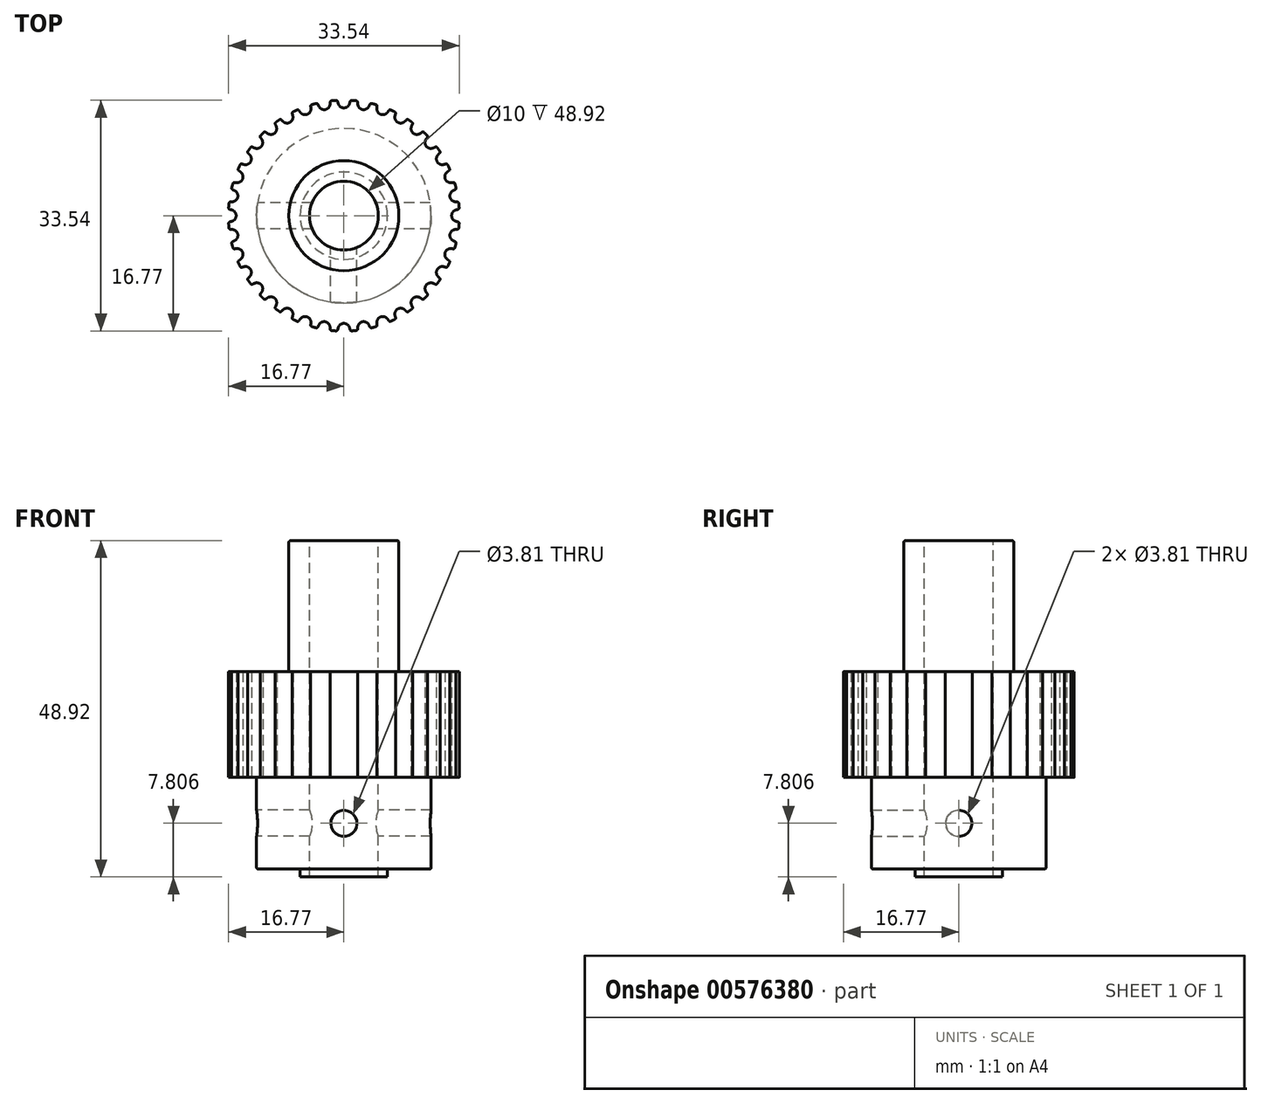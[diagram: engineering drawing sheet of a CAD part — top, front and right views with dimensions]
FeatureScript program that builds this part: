
annotation { "Feature Type Name" : "Feature", "Feature Type Description" : "" }
export const myFeature = defineFeature(function(context is Context, id is Id, definition is map)
    precondition{}
    {
        {
            assignVariable(context, id + "F0", {"name" : "teeth", "anyValue" : 36});
        }
        {
            assignVariable(context, id + "F1", {"name" : "width", "anyValue" : 15.4 * mm});
        }
        {
            var Q0;
            Q0=qCreatedBy(makeId("Top.planeOp"),FACE);
            var sketch = newSketch(context, id + "F2", { "sketchPlane" : qUnion([Q0])});
            skLineSegment(sketch, "E0", {"start": v(0, 0) * mm, "end": v(0, 15.67) * mm, "construction": true});
            skArc(sketch, "E1", {"start": v(4.3, 16.25) * mm, "mid": v(0, 16.8) * mm, "end": v(-4.3, 16.25) * mm, "construction": true});
            skArc(sketch, "E2", {"start": v(0, 15.67) * mm, "mid": v(0.46, 15.8) * mm, "end": v(0.77, 16.17) * mm});
            skLineSegment(sketch, "E3", {"start": v(0, 15.67) * mm, "end": v(0, 16.8) * mm, "construction": true});
            skLineSegment(sketch, "E4", {"start": v(0, 16.8) * mm, "end": v(0, 17.19) * mm, "construction": true});
            skArc(sketch, "E5", {"start": v(1.5, 17.12) * mm, "mid": v(0, 17.19) * mm, "end": v(-1.5, 17.12) * mm, "construction": true});
            skLineSegment(sketch, "E6", {"start": v(1.46, 16.74) * mm, "end": v(0, 0) * mm});
            skLineSegment(sketch, "E7", {"start": v(0, 0) * mm, "end": v(-1.46, 16.74) * mm});
            skArc(sketch, "E8", {"start": v(1.16, 16.77) * mm, "mid": v(0.98, 16.71) * mm, "end": v(0.9, 16.56) * mm});
            skArc(sketch, "E9", {"start": v(0.77, 16.17) * mm, "mid": v(0.85, 16.36) * mm, "end": v(0.9, 16.56) * mm});
            skArc(sketch, "E10.MirrorCS", {"start": v(0, 15.67) * mm, "mid": v(-0.46, 15.8) * mm, "end": v(-0.77, 16.17) * mm});
            skArc(sketch, "E11.MirrorCS", {"start": v(-0.77, 16.17) * mm, "mid": v(-0.85, 16.36) * mm, "end": v(-0.9, 16.56) * mm});
            skArc(sketch, "E12.MirrorCS", {"start": v(-1.16, 16.77) * mm, "mid": v(-0.98, 16.71) * mm, "end": v(-0.9, 16.56) * mm});
            skArc(sketch, "E13", {"start": v(0, 16.8) * mm, "mid": v(-0.3, 16.8) * mm, "end": v(-0.6, 16.8) * mm, "construction": true});
            skArc(sketch, "E14", {"start": v(4.23, 15.09) * mm, "mid": v(0, 15.67) * mm, "end": v(-4.23, 15.09) * mm, "construction": true});
            skArc(sketch, "E15", {"start": v(-1.16, 16.77) * mm, "mid": v(-1.31, 16.76) * mm, "end": v(-1.46, 16.74) * mm});
            skArc(sketch, "E16", {"start": v(1.16, 16.77) * mm, "mid": v(1.31, 16.76) * mm, "end": v(1.46, 16.74) * mm});
            skPoint(sketch, "E17", {"position": v(0, 15.67) * mm});
            skSolve(sketch);
        }
        {
            var Q0;
            Q0=makeQuery(id+"F2.imprint","IMPRINT",FACE,{"disambiguationData":[TD([[makeQuery(id+"F2.imprint","IMPRINT",EDGE,{"derivedFrom":sQuery(id+"F2.wireOp",EDGE,"E2")}),-1.0]])]});
            var Q1;
            {var subQ1=sQuery(id+"F2.wireOp",EDGE,"N9a9pOVT-NxnP-9PMo-Yz0L-ytRW1WlfzG62");Q1=makeQuery(id+"F2.imprint","IMPRINT",FACE,{"disambiguationData":[TD([[makeQuery(id+"F2.imprint","IMPRINT",EDGE,{"derivedFrom":subQ1}),-1.0]])]});}
            var Q2;
            {var subQ0=sQuery(id+"F2.wireOp",EDGE,"E6");Q2=makeQuery(id+"F2.imprint","IMPRINT",FACE,{"disambiguationData":[TD([[makeQuery(id+"F2.imprint","IMPRINT",EDGE,{"derivedFrom":subQ0}),-1.0]])]});}
            extrude(context, id + "F3", {"entities" : qUnion([Q0, Q1, Q2]), "depth" : (getVariable(context, 'width')), "offsetDistance" : 25 * mm, "symmetric" : true});
        }
        {
            var Q0;
            Q0=makeQuery(id+"F3.opExtrude","SWEPT_BODY",BODY,{"disambiguationData":[OSD([sQuery(id+"F2.wireOp",EDGE,"E1"),sQuery(id+"F2.wireOp",EDGE,"E2"),sQuery(id+"F2.wireOp",EDGE,"WtW3y5By-gfdo-wMA2-XeKf-OYMCoWhlFWBV"),sQuery(id+"F2.wireOp",EDGE,"E6"),sQuery(id+"F2.wireOp",EDGE,"E7"),sQuery(id+"F2.wireOp",EDGE,"N9a9pOVT-NxnP-9PMo-Yz0L-ytRW1WlfzG62"),sQuery(id+"F2.wireOp",EDGE,"E8"),sQuery(id+"F2.wireOp",EDGE,"E9"),sQuery(id+"F2.wireOp",EDGE,"E10.MirrorCS"),sQuery(id+"F2.wireOp",EDGE,"E11.MirrorCS"),sQuery(id+"F2.wireOp",EDGE,"E12.MirrorCS")])]});
            var Q1;
            Q1=makeQuery(id+"F3.opExtrude","SWEPT_EDGE",EDGE,{"disambiguationData":[OSD([sQuery(id+"F2.wireOp",EDGE,"E6"),sQuery(id+"F2.wireOp",EDGE,"E7")])]});
            circularPattern(context, id + "F4", {"operationType" : NewBodyOperationType.ADD, "entities" : qUnion([Q0]), "axis" : qUnion([Q1]), "angle" : 360 * degree, "instanceCount" : getVariable(context, 'teeth'), "equalSpace" : true, "computeTransformsWithoutBuiltin" : true});
        }
        {
            var Q0;
            {var subQ0=makeQuery(id+"F3.opExtrude","CAP_FACE",FACE,{"disambiguationData":[OSD([sQuery(id+"F2.wireOp",EDGE,"E2"),sQuery(id+"F2.wireOp",EDGE,"E6"),sQuery(id+"F2.wireOp",EDGE,"E7"),sQuery(id+"F2.wireOp",EDGE,"E8"),sQuery(id+"F2.wireOp",EDGE,"E9"),sQuery(id+"F2.wireOp",EDGE,"E10.MirrorCS"),sQuery(id+"F2.wireOp",EDGE,"E11.MirrorCS"),sQuery(id+"F2.wireOp",EDGE,"E12.MirrorCS"),sQuery(id+"F2.wireOp",EDGE,"E15"),sQuery(id+"F2.wireOp",EDGE,"E16")])],"isStart":true});Q0=makeQuery(id+"F4.boolean.opBoolean","MERGE",FACE,{"derivedFrom":[subQ0,makeQuery(id+"F4.opPattern","COPY",FACE,{"derivedFrom":subQ0,"instanceName":"1"}),makeQuery(id+"F4.opPattern","COPY",FACE,{"derivedFrom":subQ0,"instanceName":"2"}),makeQuery(id+"F4.opPattern","COPY",FACE,{"derivedFrom":subQ0,"instanceName":"3"}),makeQuery(id+"F4.opPattern","COPY",FACE,{"derivedFrom":subQ0,"instanceName":"4"}),makeQuery(id+"F4.opPattern","COPY",FACE,{"derivedFrom":subQ0,"instanceName":"5"}),makeQuery(id+"F4.opPattern","COPY",FACE,{"derivedFrom":subQ0,"instanceName":"6"}),makeQuery(id+"F4.opPattern","COPY",FACE,{"derivedFrom":subQ0,"instanceName":"7"}),makeQuery(id+"F4.opPattern","COPY",FACE,{"derivedFrom":subQ0,"instanceName":"8"}),makeQuery(id+"F4.opPattern","COPY",FACE,{"derivedFrom":subQ0,"instanceName":"9"}),makeQuery(id+"F4.opPattern","COPY",FACE,{"derivedFrom":subQ0,"instanceName":"10"}),makeQuery(id+"F4.opPattern","COPY",FACE,{"derivedFrom":subQ0,"instanceName":"11"}),makeQuery(id+"F4.opPattern","COPY",FACE,{"derivedFrom":subQ0,"instanceName":"12"}),makeQuery(id+"F4.opPattern","COPY",FACE,{"derivedFrom":subQ0,"instanceName":"13"}),makeQuery(id+"F4.opPattern","COPY",FACE,{"derivedFrom":subQ0,"instanceName":"14"}),makeQuery(id+"F4.opPattern","COPY",FACE,{"derivedFrom":subQ0,"instanceName":"15"}),makeQuery(id+"F4.opPattern","COPY",FACE,{"derivedFrom":subQ0,"instanceName":"16"}),makeQuery(id+"F4.opPattern","COPY",FACE,{"derivedFrom":subQ0,"instanceName":"17"}),makeQuery(id+"F4.opPattern","COPY",FACE,{"derivedFrom":subQ0,"instanceName":"18"}),makeQuery(id+"F4.opPattern","COPY",FACE,{"derivedFrom":subQ0,"instanceName":"19"}),makeQuery(id+"F4.opPattern","COPY",FACE,{"derivedFrom":subQ0,"instanceName":"20"}),makeQuery(id+"F4.opPattern","COPY",FACE,{"derivedFrom":subQ0,"instanceName":"21"}),makeQuery(id+"F4.opPattern","COPY",FACE,{"derivedFrom":subQ0,"instanceName":"22"}),makeQuery(id+"F4.opPattern","COPY",FACE,{"derivedFrom":subQ0,"instanceName":"23"}),makeQuery(id+"F4.opPattern","COPY",FACE,{"derivedFrom":subQ0,"instanceName":"24"}),makeQuery(id+"F4.opPattern","COPY",FACE,{"derivedFrom":subQ0,"instanceName":"25"}),makeQuery(id+"F4.opPattern","COPY",FACE,{"derivedFrom":subQ0,"instanceName":"26"}),makeQuery(id+"F4.opPattern","COPY",FACE,{"derivedFrom":subQ0,"instanceName":"27"}),makeQuery(id+"F4.opPattern","COPY",FACE,{"derivedFrom":subQ0,"instanceName":"28"}),makeQuery(id+"F4.opPattern","COPY",FACE,{"derivedFrom":subQ0,"instanceName":"29"}),makeQuery(id+"F4.opPattern","COPY",FACE,{"derivedFrom":subQ0,"instanceName":"30"}),makeQuery(id+"F4.opPattern","COPY",FACE,{"derivedFrom":subQ0,"instanceName":"31"}),makeQuery(id+"F4.opPattern","COPY",FACE,{"derivedFrom":subQ0,"instanceName":"32"}),makeQuery(id+"F4.opPattern","COPY",FACE,{"derivedFrom":subQ0,"instanceName":"33"}),makeQuery(id+"F4.opPattern","COPY",FACE,{"derivedFrom":subQ0,"instanceName":"34"}),makeQuery(id+"F4.opPattern","COPY",FACE,{"derivedFrom":subQ0,"instanceName":"35"})]});}
            var sketch = newSketch(context, id + "F5", { "sketchPlane" : qUnion([Q0])});
            skCircle(sketch, "E18", {"center": v(0, 0) * mm, "radius": 12.7 * mm});
            skSolve(sketch);
        }
        {
            var Q0;
            Q0=qSketchRegion(id+"F5",true);
            extrude(context, id + "F6", {"entities" : qUnion([Q0]), "operationType" : NewBodyOperationType.ADD, "depth" : 13.33 * mm, "offsetDistance" : 25 * mm});
        }
        {
            var Q0;
            Q0=makeQuery(id+"F6.opExtrude","CAP_FACE",FACE,{"disambiguationData":[OSD([sQuery(id+"F5.wireOp",EDGE,"E18")])],"isStart":false});
            var sketch = newSketch(context, id + "F7", { "sketchPlane" : qUnion([Q0])});
            skCircle(sketch, "E19", {"center": v(0, 0) * mm, "radius": 6.35 * mm});
            skSolve(sketch);
        }
        {
            var Q0;
            Q0 = qSketchRegion(id + "F7", true);
            extrude(context, id + "F8", {"entities" : qUnion([Q0]), "operationType" : NewBodyOperationType.ADD, "depth" : 1.14 * mm, "offsetDistance" : 25 * mm});
        }
        {
            var Q0;
            Q0=qCreatedBy(makeId("Front.planeOp"),FACE);
            var sketch = newSketch(context, id + "F9", { "sketchPlane" : qUnion([Q0])});
            skCircle(sketch, "E20", {"center": v(0, -14.36) * mm, "radius": 1.9 * mm});
            skSolve(sketch);
        }
        {
            var Q0;
            Q0=qSketchRegion(id+"F9",true);
            extrude(context, id + "F10", {"entities" : qUnion([Q0]), "operationType" : NewBodyOperationType.REMOVE, "endBound" : BoundingType.THROUGH_ALL, "depth" : 25 * mm, "offsetDistance" : 25 * mm});
        }
        {
            var Q0;
            Q0=qCreatedBy(makeId("Right.planeOp"),FACE);
            var sketch = newSketch(context, id + "F11", { "sketchPlane" : qUnion([Q0])});
            skCircle(sketch, "E21", {"center": v(0, -14.36) * mm, "radius": 1.9 * mm});
            skSolve(sketch);
        }
        {
            var Q0;
            Q0=qSketchRegion(id+"F11",true);
            extrude(context, id + "F12", {"entities" : qUnion([Q0]), "operationType" : NewBodyOperationType.REMOVE, "depth" : 26 * mm, "offsetDistance" : 25 * mm, "symmetric" : true});
        }
        {
            var Q0;
            {var subQ0=makeQuery(id+"F3.opExtrude","CAP_FACE",FACE,{"disambiguationData":[OSD([sQuery(id+"F2.wireOp",EDGE,"E2"),sQuery(id+"F2.wireOp",EDGE,"E6"),sQuery(id+"F2.wireOp",EDGE,"E7"),sQuery(id+"F2.wireOp",EDGE,"E8"),sQuery(id+"F2.wireOp",EDGE,"E9"),sQuery(id+"F2.wireOp",EDGE,"E10.MirrorCS"),sQuery(id+"F2.wireOp",EDGE,"E11.MirrorCS"),sQuery(id+"F2.wireOp",EDGE,"E12.MirrorCS"),sQuery(id+"F2.wireOp",EDGE,"E15"),sQuery(id+"F2.wireOp",EDGE,"E16")])],"isStart":false});Q0=makeQuery(id+"F4.boolean.opBoolean","MERGE",FACE,{"derivedFrom":[subQ0,makeQuery(id+"F4.opPattern","COPY",FACE,{"derivedFrom":subQ0,"instanceName":"1"}),makeQuery(id+"F4.opPattern","COPY",FACE,{"derivedFrom":subQ0,"instanceName":"2"}),makeQuery(id+"F4.opPattern","COPY",FACE,{"derivedFrom":subQ0,"instanceName":"3"}),makeQuery(id+"F4.opPattern","COPY",FACE,{"derivedFrom":subQ0,"instanceName":"4"}),makeQuery(id+"F4.opPattern","COPY",FACE,{"derivedFrom":subQ0,"instanceName":"5"}),makeQuery(id+"F4.opPattern","COPY",FACE,{"derivedFrom":subQ0,"instanceName":"6"}),makeQuery(id+"F4.opPattern","COPY",FACE,{"derivedFrom":subQ0,"instanceName":"7"}),makeQuery(id+"F4.opPattern","COPY",FACE,{"derivedFrom":subQ0,"instanceName":"8"}),makeQuery(id+"F4.opPattern","COPY",FACE,{"derivedFrom":subQ0,"instanceName":"9"}),makeQuery(id+"F4.opPattern","COPY",FACE,{"derivedFrom":subQ0,"instanceName":"10"}),makeQuery(id+"F4.opPattern","COPY",FACE,{"derivedFrom":subQ0,"instanceName":"11"}),makeQuery(id+"F4.opPattern","COPY",FACE,{"derivedFrom":subQ0,"instanceName":"12"}),makeQuery(id+"F4.opPattern","COPY",FACE,{"derivedFrom":subQ0,"instanceName":"13"}),makeQuery(id+"F4.opPattern","COPY",FACE,{"derivedFrom":subQ0,"instanceName":"14"}),makeQuery(id+"F4.opPattern","COPY",FACE,{"derivedFrom":subQ0,"instanceName":"15"}),makeQuery(id+"F4.opPattern","COPY",FACE,{"derivedFrom":subQ0,"instanceName":"16"}),makeQuery(id+"F4.opPattern","COPY",FACE,{"derivedFrom":subQ0,"instanceName":"17"}),makeQuery(id+"F4.opPattern","COPY",FACE,{"derivedFrom":subQ0,"instanceName":"18"}),makeQuery(id+"F4.opPattern","COPY",FACE,{"derivedFrom":subQ0,"instanceName":"19"}),makeQuery(id+"F4.opPattern","COPY",FACE,{"derivedFrom":subQ0,"instanceName":"20"}),makeQuery(id+"F4.opPattern","COPY",FACE,{"derivedFrom":subQ0,"instanceName":"21"}),makeQuery(id+"F4.opPattern","COPY",FACE,{"derivedFrom":subQ0,"instanceName":"22"}),makeQuery(id+"F4.opPattern","COPY",FACE,{"derivedFrom":subQ0,"instanceName":"23"}),makeQuery(id+"F4.opPattern","COPY",FACE,{"derivedFrom":subQ0,"instanceName":"24"}),makeQuery(id+"F4.opPattern","COPY",FACE,{"derivedFrom":subQ0,"instanceName":"25"}),makeQuery(id+"F4.opPattern","COPY",FACE,{"derivedFrom":subQ0,"instanceName":"26"}),makeQuery(id+"F4.opPattern","COPY",FACE,{"derivedFrom":subQ0,"instanceName":"27"}),makeQuery(id+"F4.opPattern","COPY",FACE,{"derivedFrom":subQ0,"instanceName":"28"}),makeQuery(id+"F4.opPattern","COPY",FACE,{"derivedFrom":subQ0,"instanceName":"29"}),makeQuery(id+"F4.opPattern","COPY",FACE,{"derivedFrom":subQ0,"instanceName":"30"}),makeQuery(id+"F4.opPattern","COPY",FACE,{"derivedFrom":subQ0,"instanceName":"31"}),makeQuery(id+"F4.opPattern","COPY",FACE,{"derivedFrom":subQ0,"instanceName":"32"}),makeQuery(id+"F4.opPattern","COPY",FACE,{"derivedFrom":subQ0,"instanceName":"33"}),makeQuery(id+"F4.opPattern","COPY",FACE,{"derivedFrom":subQ0,"instanceName":"34"}),makeQuery(id+"F4.opPattern","COPY",FACE,{"derivedFrom":subQ0,"instanceName":"35"})]});}
            var sketch = newSketch(context, id + "F13", { "sketchPlane" : qUnion([Q0])});
            skCircle(sketch, "E22", {"center": v(0, 0) * mm, "radius": 8 * mm});
            skSolve(sketch);
        }
        {
            var Q0;
            Q0 = qSketchRegion(id + "F13", true);
            extrude(context, id + "F14", {"entities" : qUnion([Q0]), "operationType" : NewBodyOperationType.ADD, "depth" : 19.05 * mm, "offsetDistance" : 25 * mm});
        }
        {
            var Q0;
            Q0=makeQuery(id+"F14.opExtrude","CAP_FACE",FACE,{"disambiguationData":[OSD([sQuery(id+"F13.wireOp",EDGE,"E22")])],"isStart":false});
            var sketch = newSketch(context, id + "F15", { "sketchPlane" : qUnion([Q0])});
            skCircle(sketch, "E23", {"center": v(0, 0) * mm, "radius": 5 * mm});
            skSolve(sketch);
        }
        {
            var Q0;
            Q0=qSketchRegion(id+"F15",true);
            extrude(context, id + "F16", {"entities" : qUnion([Q0]), "operationType" : NewBodyOperationType.REMOVE, "endBound" : BoundingType.THROUGH_ALL, "oppositeDirection" : true, "depth" : 25 * mm, "offsetDistance" : 25 * mm});
        }
        {
            var Q0;
            Q0=makeQuery(id+"F6.opExtrude","CAP_EDGE",EDGE,{"disambiguationData":[OSD([sQuery(id+"F5.wireOp",EDGE,"E18")])],"isStart":false});
            var Q1;
            Q1=makeQuery(id+"F14.opExtrude","CAP_EDGE",EDGE,{"disambiguationData":[OSD([sQuery(id+"F13.wireOp",EDGE,"E22")])],"isStart":false});
            fillet(context, id + "F17", {"entities" : qUnion([Q0, Q1]), "radius" : 0.25 * mm, "tangentPropagation" : true, "allowEdgeOverflow" : false});
        }
    });
